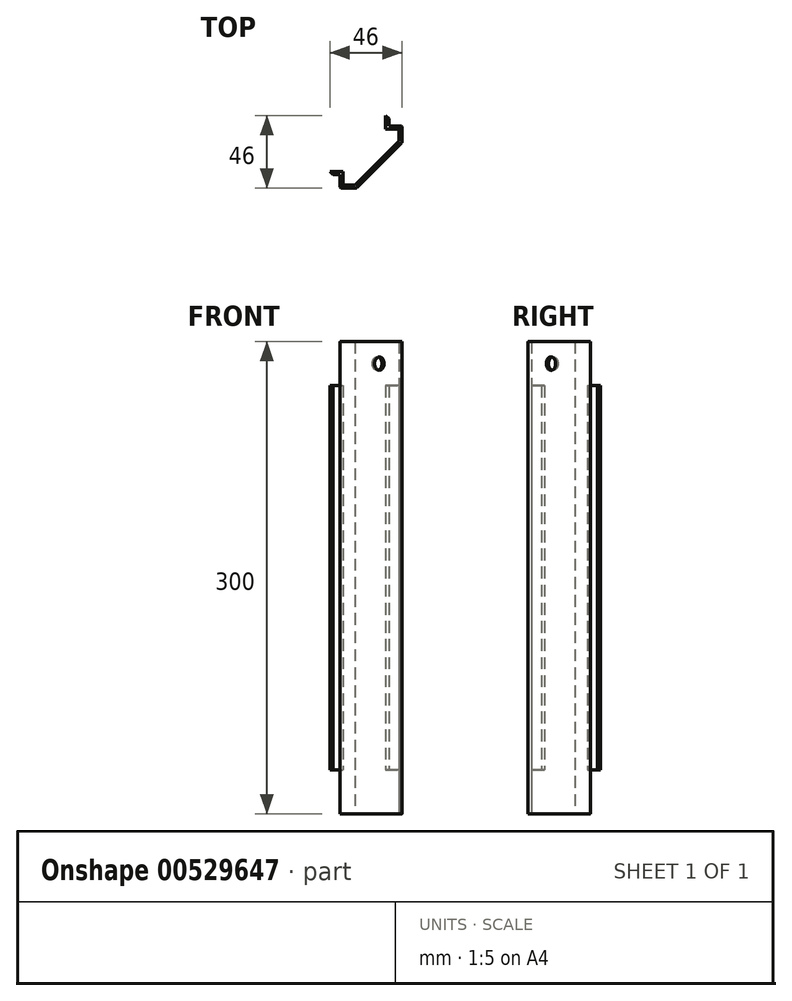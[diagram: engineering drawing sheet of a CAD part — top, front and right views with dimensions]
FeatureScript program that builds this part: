
annotation { "Feature Type Name" : "Feature", "Feature Type Description" : "" }
export const myFeature = defineFeature(function(context is Context, id is Id, definition is map)
    precondition{}
    {
        {
            var Q0;
            Q0=qCreatedBy(makeId("Top.planeOp"),FACE);
            var sketch = newSketch(context, id + "F0", { "sketchPlane" : qUnion([Q0])});
            skLineSegment(sketch, "E0", {"start": v(-68.1, 0) * mm, "end": v(72.16, 0) * mm, "construction": true});
            skLineSegment(sketch, "E1", {"start": v(0, 70.28) * mm, "end": v(0, -61.88) * mm, "construction": true});
            skLineSegment(sketch, "E2.bottom", {"start": v(-19.75, 19.75) * mm, "end": v(19.75, 19.75) * mm, "construction": true});
            skLineSegment(sketch, "E2.top", {"start": v(-19.75, -19.75) * mm, "end": v(19.75, -19.75) * mm, "construction": true});
            skLineSegment(sketch, "E2.left", {"start": v(-19.75, 19.75) * mm, "end": v(-19.75, -19.75) * mm, "construction": true});
            skLineSegment(sketch, "E2.right", {"start": v(19.75, 19.75) * mm, "end": v(19.75, -19.75) * mm, "construction": true});
            skLineSegment(sketch, "E3", {"start": v(-19.75, -19.75) * mm, "end": v(-9.25, -19.75) * mm});
            skLineSegment(sketch, "E4", {"start": v(19.75, 19.75) * mm, "end": v(19.75, 9.25) * mm});
            skLineSegment(sketch, "E5", {"start": v(-9.25, -19.75) * mm, "end": v(19.75, 9.25) * mm});
            skLineSegment(sketch, "E6.0", {"start": v(-19.75, -17.75) * mm, "end": v(-10.08, -17.75) * mm});
            skLineSegment(sketch, "E6.1", {"start": v(-10.08, -17.75) * mm, "end": v(17.75, 10.08) * mm});
            skLineSegment(sketch, "E6.2", {"start": v(17.75, 19.75) * mm, "end": v(17.75, 10.08) * mm});
            skLineSegment(sketch, "E7", {"start": v(-19.75, -19.75) * mm, "end": v(-19.75, -17.75) * mm});
            skLineSegment(sketch, "E8", {"start": v(19.75, 19.75) * mm, "end": v(17.75, 19.75) * mm});
            skSolve(sketch);
        }
        {
            var Q0;
            Q0=qSketchRegion(id+"F0",true);
            extrude(context, id + "F1", {"entities" : qUnion([Q0]), "depth" : 28 * mm});
        }
        {
            var Q0;
            Q0=makeQuery(id+"F1.opExtrude","CAP_FACE",FACE,{"disambiguationData":[OSD([sQuery(id+"F0.wireOp",EDGE,"E3"),sQuery(id+"F0.wireOp",EDGE,"E4"),sQuery(id+"F0.wireOp",EDGE,"E5"),sQuery(id+"F0.wireOp",EDGE,"E6.0"),sQuery(id+"F0.wireOp",EDGE,"E6.1"),sQuery(id+"F0.wireOp",EDGE,"E6.2"),sQuery(id+"F0.wireOp",EDGE,"E7"),sQuery(id+"F0.wireOp",EDGE,"E8")])],"isStart":false});
            var sketch = newSketch(context, id + "F2", { "sketchPlane" : qUnion([Q0])});
            skLineSegment(sketch, "E9.1", {"start": v(-9.25, -19.75) * mm, "end": v(19.75, 9.25) * mm});
            skLineSegment(sketch, "E9.2", {"start": v(19.75, 19.75) * mm, "end": v(19.75, 9.25) * mm});
            skLineSegment(sketch, "E10", {"start": v(19.75, 19.75) * mm, "end": v(11.25, 19.75) * mm});
            skLineSegment(sketch, "E11", {"start": v(17.75, 17.75) * mm, "end": v(17.75, 10.08) * mm});
            skLineSegment(sketch, "E12", {"start": v(17.75, 10.08) * mm, "end": v(16.59, 8.91) * mm});
            skLineSegment(sketch, "E13.left", {"start": v(11.25, 19.75) * mm, "end": v(11.25, 24.25) * mm});
            skLineSegment(sketch, "E14", {"start": v(11.25, 24.25) * mm, "end": v(9.25, 26.25) * mm});
            skLineSegment(sketch, "E15.trimOffspring", {"start": v(16.59, 8.91) * mm, "end": v(-8.91, -16.59) * mm});
            skLineSegment(sketch, "E16.0", {"start": v(9.25, 19.75) * mm, "end": v(9.25, 23.42) * mm});
            skLineSegment(sketch, "E17.0", {"start": v(9.25, 23.42) * mm, "end": v(9.25, 23.42) * mm});
            skLineSegment(sketch, "E18.trimOffspring", {"start": v(9.25, 23.42) * mm, "end": v(9.25, 26.25) * mm});
            skLineSegment(sketch, "E19", {"start": v(0, 0) * mm, "end": v(5.25, -5.25) * mm, "construction": true});
            skLineSegment(sketch, "E20.MirrorCS", {"start": v(-19.75, -9.25) * mm, "end": v(-23.42, -9.25) * mm});
            skLineSegment(sketch, "E21.MirrorCS", {"start": v(-19.75, -11.25) * mm, "end": v(-24.25, -11.25) * mm});
            skLineSegment(sketch, "E22.MirrorCS", {"start": v(-23.42, -9.25) * mm, "end": v(-26.25, -9.25) * mm});
            skLineSegment(sketch, "E23.MirrorCS", {"start": v(-19.75, -19.75) * mm, "end": v(-9.25, -19.75) * mm});
            skLineSegment(sketch, "E24.MirrorCS", {"start": v(-10.08, -17.75) * mm, "end": v(-8.91, -16.59) * mm});
            skLineSegment(sketch, "E25.MirrorCS", {"start": v(-24.25, -11.25) * mm, "end": v(-26.25, -9.25) * mm});
            skLineSegment(sketch, "E26.MirrorCS", {"start": v(-17.75, -17.75) * mm, "end": v(-10.08, -17.75) * mm});
            skLineSegment(sketch, "E27.MirrorCS", {"start": v(-23.42, -9.25) * mm, "end": v(-23.42, -9.25) * mm});
            skLineSegment(sketch, "E28.MirrorCS", {"start": v(-19.75, -19.75) * mm, "end": v(-19.75, -11.25) * mm});
            skLineSegment(sketch, "E29.trimOffspring", {"start": v(-8.91, -16.59) * mm, "end": v(-10.08, -17.75) * mm});
            skLineSegment(sketch, "E30", {"start": v(9.25, 19.75) * mm, "end": v(9.25, 17.75) * mm});
            skLineSegment(sketch, "E31", {"start": v(9.25, 17.75) * mm, "end": v(17.75, 17.75) * mm});
            skLineSegment(sketch, "E32", {"start": v(-19.75, -9.25) * mm, "end": v(-17.75, -9.25) * mm});
            skLineSegment(sketch, "E33", {"start": v(-17.75, -9.25) * mm, "end": v(-17.75, -17.75) * mm});
            skSolve(sketch);
        }
        {
            var Q0;
            Q0=qSketchRegion(id+"F2",true);
            extrude(context, id + "F3", {"entities" : qUnion([Q0]), "operationType" : NewBodyOperationType.ADD, "depth" : 244 * mm, "offsetDistance" : 25 * mm});
        }
        {
            var Q0;
            Q0=makeQuery(id+"F3.opExtrude","CAP_FACE",FACE,{"disambiguationData":[OSD([sQuery(id+"F2.wireOp",EDGE,"E9.1"),sQuery(id+"F2.wireOp",EDGE,"E9.2"),sQuery(id+"F2.wireOp",EDGE,"E10"),sQuery(id+"F2.wireOp",EDGE,"E11"),sQuery(id+"F2.wireOp",EDGE,"E12"),sQuery(id+"F2.wireOp",EDGE,"E13.left"),sQuery(id+"F2.wireOp",EDGE,"E14"),sQuery(id+"F2.wireOp",EDGE,"E15.trimOffspring"),sQuery(id+"F2.wireOp",EDGE,"E16.0"),sQuery(id+"F2.wireOp",EDGE,"E17.0"),sQuery(id+"F2.wireOp",EDGE,"E18.trimOffspring"),sQuery(id+"F2.wireOp",EDGE,"E20.MirrorCS"),sQuery(id+"F2.wireOp",EDGE,"E21.MirrorCS"),sQuery(id+"F2.wireOp",EDGE,"E22.MirrorCS"),sQuery(id+"F2.wireOp",EDGE,"E23.MirrorCS"),sQuery(id+"F2.wireOp",EDGE,"E25.MirrorCS"),sQuery(id+"F2.wireOp",EDGE,"E26.MirrorCS"),sQuery(id+"F2.wireOp",EDGE,"E27.MirrorCS"),sQuery(id+"F2.wireOp",EDGE,"E28.MirrorCS"),sQuery(id+"F2.wireOp",EDGE,"E29.trimOffspring"),sQuery(id+"F2.wireOp",EDGE,"E30"),sQuery(id+"F2.wireOp",EDGE,"E31"),sQuery(id+"F2.wireOp",EDGE,"E32"),sQuery(id+"F2.wireOp",EDGE,"E33")])],"isStart":false});
            var sketch = newSketch(context, id + "F4", { "sketchPlane" : qUnion([Q0])});
            skLineSegment(sketch, "E34.0.0", {"start": v(19.75, 19.75) * mm, "end": v(19.75, 9.25) * mm});
            skLineSegment(sketch, "E34.0.1", {"start": v(19.75, 9.25) * mm, "end": v(-9.25, -19.75) * mm});
            skLineSegment(sketch, "E34.0.2", {"start": v(-9.25, -19.75) * mm, "end": v(-19.75, -19.75) * mm});
            skLineSegment(sketch, "E34.0.3", {"start": v(-19.75, -19.75) * mm, "end": v(-19.75, -17.75) * mm});
            skLineSegment(sketch, "E34.0.4", {"start": v(-19.75, -17.75) * mm, "end": v(-10.08, -17.75) * mm});
            skLineSegment(sketch, "E34.0.5", {"start": v(-10.08, -17.75) * mm, "end": v(17.75, 10.08) * mm});
            skLineSegment(sketch, "E34.0.6", {"start": v(17.75, 10.08) * mm, "end": v(17.75, 19.75) * mm});
            skLineSegment(sketch, "E34.0.7", {"start": v(17.75, 19.75) * mm, "end": v(19.75, 19.75) * mm});
            skSolve(sketch);
        }
        {
            var Q0;
            Q0=qSketchRegion(id+"F4",true);
            extrude(context, id + "F5", {"entities" : qUnion([Q0]), "operationType" : NewBodyOperationType.ADD, "depth" : 28 * mm});
        }
        {
            var Q0;
            Q0=makeQuery(id+"F5.boolean.opBoolean","MERGE",EDGE,{"derivedFrom":[makeQuery(id+"F3.boolean.opBoolean","MERGE",EDGE,{"derivedFrom":[makeQuery(id+"F1.opExtrude","SWEPT_EDGE",EDGE,{"disambiguationData":[OSD([sQuery(id+"F0.wireOp",EDGE,"E4"),sQuery(id+"F0.wireOp",EDGE,"E5")])]}),makeQuery(id+"F3.opExtrude","SWEPT_EDGE",EDGE,{"disambiguationData":[OSD([sQuery(id+"F2.wireOp",EDGE,"E9.1"),sQuery(id+"F2.wireOp",EDGE,"E9.2")])]})]}),makeQuery(id+"F5.opExtrude","SWEPT_EDGE",EDGE,{"disambiguationData":[OSD([sQuery(id+"F4.wireOp",EDGE,"E34.0.0"),sQuery(id+"F4.wireOp",EDGE,"E34.0.1")])]})]});
            var Q1;
            Q1=makeQuery(id+"F5.boolean.opBoolean","MERGE",EDGE,{"derivedFrom":[makeQuery(id+"F3.boolean.opBoolean","MERGE",EDGE,{"derivedFrom":[makeQuery(id+"F1.opExtrude","SWEPT_EDGE",EDGE,{"disambiguationData":[OSD([sQuery(id+"F0.wireOp",EDGE,"E3"),sQuery(id+"F0.wireOp",EDGE,"E5")])]}),makeQuery(id+"F3.opExtrude","SWEPT_EDGE",EDGE,{"disambiguationData":[OSD([sQuery(id+"F2.wireOp",EDGE,"E9.1"),sQuery(id+"F2.wireOp",EDGE,"E23.MirrorCS")])]})]}),makeQuery(id+"F5.opExtrude","SWEPT_EDGE",EDGE,{"disambiguationData":[OSD([sQuery(id+"F4.wireOp",EDGE,"E34.0.1"),sQuery(id+"F4.wireOp",EDGE,"E34.0.2")])]})]});
            fillet(context, id + "F6", {"entities" : qUnion([Q0, Q1]), "radius" : 2 * mm, "tangentPropagation" : true, "allowEdgeOverflow" : false});
        }
        {
            var Q0;
            Q0=makeQuery(id+"F5.boolean.opBoolean","MERGE",EDGE,{"derivedFrom":[makeQuery(id+"F3.boolean.opBoolean","MERGE",EDGE,{"derivedFrom":[makeQuery(id+"F1.opExtrude","SWEPT_EDGE",EDGE,{"disambiguationData":[OSD([sQuery(id+"F0.wireOp",EDGE,"E3"),sQuery(id+"F0.wireOp",EDGE,"E7")])]}),makeQuery(id+"F3.opExtrude","SWEPT_EDGE",EDGE,{"disambiguationData":[OSD([sQuery(id+"F2.wireOp",EDGE,"E23.MirrorCS"),sQuery(id+"F2.wireOp",EDGE,"E28.MirrorCS")])]})]}),makeQuery(id+"F5.opExtrude","SWEPT_EDGE",EDGE,{"disambiguationData":[OSD([sQuery(id+"F4.wireOp",EDGE,"E34.0.2"),sQuery(id+"F4.wireOp",EDGE,"E34.0.3")])]})]});
            var Q1;
            Q1=makeQuery(id+"F5.boolean.opBoolean","MERGE",EDGE,{"derivedFrom":[makeQuery(id+"F3.boolean.opBoolean","MERGE",EDGE,{"derivedFrom":[makeQuery(id+"F1.opExtrude","SWEPT_EDGE",EDGE,{"disambiguationData":[OSD([sQuery(id+"F0.wireOp",EDGE,"E4"),sQuery(id+"F0.wireOp",EDGE,"E8")])]}),makeQuery(id+"F3.opExtrude","SWEPT_EDGE",EDGE,{"disambiguationData":[OSD([sQuery(id+"F2.wireOp",EDGE,"E9.2"),sQuery(id+"F2.wireOp",EDGE,"E10")])]})]}),makeQuery(id+"F5.opExtrude","SWEPT_EDGE",EDGE,{"disambiguationData":[OSD([sQuery(id+"F4.wireOp",EDGE,"E34.0.0"),sQuery(id+"F4.wireOp",EDGE,"E34.0.7")])]})]});
            fillet(context, id + "F7", {"entities" : qUnion([Q0, Q1]), "radius" : 1 * mm, "tangentPropagation" : true, "allowEdgeOverflow" : false});
        }
        {
            var Q0;
            Q0=makeQuery(id+"F5.boolean.opBoolean","MERGE",FACE,{"derivedFrom":[makeQuery(id+"F3.boolean.opBoolean","MERGE",FACE,{"derivedFrom":[makeQuery(id+"F1.opExtrude","SWEPT_FACE",FACE,{"disambiguationData":[OSD([sQuery(id+"F0.wireOp",EDGE,"E5")])]}),makeQuery(id+"F3.opExtrude","SWEPT_FACE",FACE,{"disambiguationData":[OSD([sQuery(id+"F2.wireOp",EDGE,"E9.1")])]})]}),makeQuery(id+"F5.opExtrude","SWEPT_FACE",FACE,{"disambiguationData":[OSD([sQuery(id+"F4.wireOp",EDGE,"E34.0.1")])]})]});
            var sketch = newSketch(context, id + "F8", { "sketchPlane" : qUnion([Q0])});
            skLineSegment(sketch, "E35.0", {"start": v(-19.1, 272) * mm, "end": v(-25.1, 272) * mm, "construction": true});
            skLineSegment(sketch, "E36", {"start": v(-19.1, 272) * mm, "end": v(27.6, 272) * mm, "construction": true});
            skLineSegment(sketch, "E37", {"start": v(0, 300) * mm, "end": v(0, 272) * mm, "construction": true});
            skCircle(sketch, "E38", {"center": v(0, 286) * mm, "radius": 4.25 * mm});
            skSolve(sketch);
        }
        {
            var Q0;
            Q0 = qSketchRegion(id + "F8", true);
            extrude(context, id + "F9", {"entities" : qUnion([Q0]), "operationType" : NewBodyOperationType.REMOVE, "oppositeDirection" : true, "depth" : 25 * mm, "offsetDistance" : 25 * mm});
        }
    });
